# Revit family: CAME_Турникет_Скоростной_SLIDINGGATELIGHT_РаздвижнойЦентральныйМодуль550
name_source: partatom
category: Специальное оборудование
units: mm (PartAtom-declared; Revit-internal decimal feet)

## family parameters
Всегда вертикально = Да
На основе рабочей плоскости = Нет
Общий = Нет
При загрузке вырезать с полостями = Нет
Размер круглого соединителя = Использовать диаметр
Тип детали = Нормальный
Точка расчета площади = Нет

## types (1)
- CAME_Турникет_Скоростной_SLIDINGGATELIGHT_РаздвижнойЦентральныйМодуль550
    ADSK_URL документации изделия = https://camerussia.com
    ADSK_URL страницы изделия = https://camerussia.com
    ADSK_Версия Revit = 2019
    ADSK_Версия семейства = 1.0
    ADSK_Группирование = SLIDING GATE
    ADSK_Единица измерения = шт.
    ADSK_Завод-изготовитель = CAME
    ADSK_Классификация нагрузок = Прочее
    ADSK_Код изделия = Код КСР 26.30.50.119.61.2.07.09
    ADSK_Количество = 1
    ADSK_Количество фаз = 1
    ADSK_Коэффициент мощности = 0.96
    ADSK_Марка = АРТ:001SGL01C
    ADSK_Масса = 130
    ADSK_Масса_Текст = 130 кг
    ADSK_Наименование = Центральный модуль высокоскоростного раздвижного турникета SLIDING GATE LIGHT, ширина прохода 550 мм
    ADSK_Наименование краткое = Центр. модуль турникета SLIDING GATE LIGHT, 550 мм
    ADSK_Напряжение = 230 В
    ADSK_Номинальная мощность = 78 Вт
    ADSK_Обозначение = ТУ 26.30.50-001-89603926-2021
    ADSK_Полная мощность = 81 В·А
    ADSK_Размер_Высота = 1030 мм
    ADSK_Размер_Глубина = 1465 мм
    ADSK_Размер_Ширина = 875 мм
    BL_BIM library = https://bimlib.pro
    CAME_Время открывания (с) = 0.8
    CAME_Диапазон рабочих температур (°C) = -20 ÷ +68
    CAME_Интенсивность использования (%) = ИНТЕНСИВНОЕ
    CAME_Класс защиты (IP) = 44
    CAME_Максимальное количество проходов в минуту = 30
    CAME_Напряжение электропитания двигателя (В) = 24 В
    CAME_Тип механизма турникета = моторизованный
    URL = https://camerussia.com
    Группа модели = Турникеты
    Изготовитель = CAME
    Описание = Центральный модуль раздвижного турникета SLIDING GATE LIGHT для построения двух- и более проходных турникетов. Оснащен платой управления и светодиодными указателями прохода и направления.
